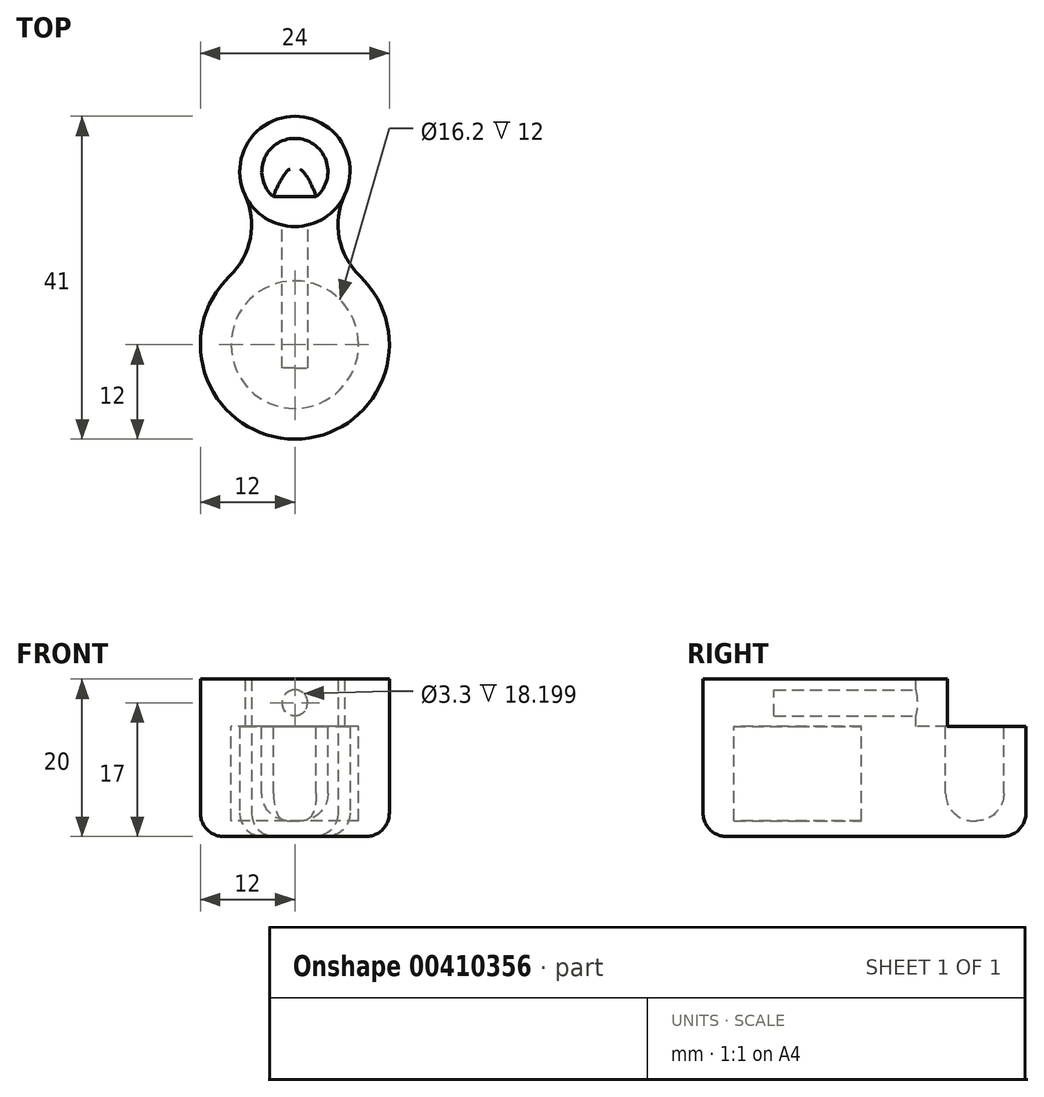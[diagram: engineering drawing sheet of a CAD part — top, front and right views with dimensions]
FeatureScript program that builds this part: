
annotation { "Feature Type Name" : "Feature", "Feature Type Description" : "" }
export const myFeature = defineFeature(function(context is Context, id is Id, definition is map)
    precondition{}
    {
        {
            var Q0;
            Q0=qCreatedBy(makeId("Top.planeOp"),FACE);
            var sketch = newSketch(context, id + "F0", { "sketchPlane" : qUnion([Q0])});
            skArc(sketch, "E0", {"start": v(0, 7) * mm, "mid": v(5.9, 3.75) * mm, "end": v(6.34, -2.97) * mm});
            skArc(sketch, "E1", {"start": v(0, -10) * mm, "mid": v(4.46, -10.86) * mm, "end": v(8.28, -13.31) * mm, "construction": true});
            skArc(sketch, "E2", {"start": v(6.34, -2.97) * mm, "mid": v(5.64, -8.46) * mm, "end": v(8.28, -13.31) * mm});
            skLineSegment(sketch, "E3", {"start": v(0, -34) * mm, "end": v(0, -10) * mm});
            skLineSegment(sketch, "E4", {"start": v(0, -10) * mm, "end": v(0, -7) * mm});
            skLineSegment(sketch, "E5", {"start": v(0, -7) * mm, "end": v(0, 7) * mm});
            skArc(sketch, "E6", {"start": v(8.28, -13.31) * mm, "mid": v(11.14, -26.46) * mm, "end": v(0, -34) * mm});
            skArc(sketch, "E7", {"start": v(6.34, -2.97) * mm, "mid": v(3.75, -5.9) * mm, "end": v(0, -7) * mm, "construction": true});
            skSolve(sketch);
        }
        {
            var Q0;
            Q0 = qSketchRegion(id + "F0", true);
            extrude(context, id + "F1", {"entities" : qUnion([Q0]), "depth" : 14 * mm});
        }
        {
            var Q0;
            Q0=makeQuery(id+"F1.opExtrude","CAP_FACE",FACE,{"disambiguationData":[OSD([sQuery(id+"F0.wireOp",EDGE,"E0"),sQuery(id+"F0.wireOp",EDGE,"E2"),sQuery(id+"F0.wireOp",EDGE,"E3"),sQuery(id+"F0.wireOp",EDGE,"E4"),sQuery(id+"F0.wireOp",EDGE,"E5"),sQuery(id+"F0.wireOp",EDGE,"E6")])],"isStart":false});
            var sketch = newSketch(context, id + "F2", { "sketchPlane" : qUnion([Q0])});
            skArc(sketch, "E8", {"start": v(0, 7) * mm, "mid": v(7, 0) * mm, "end": v(0, -7) * mm});
            skSolve(sketch);
        }
        {
            var Q0;
            {var subQ0=sQuery(id+"F2.wireOp",EDGE,"E8");var subQ3=makeQuery(id+"F2.imprint","INTERSECT",VERTEX,{"derivedFrom":[makeQuery(id+"F1.opExtrude","CAP_EDGE",EDGE,{"disambiguationData":[OSD([sQuery(id+"F0.wireOp",EDGE,"E2")])],"isStart":false}),subQ0]});Q0=makeQuery(id+"F2.imprint","IMPRINT",FACE,{"disambiguationData":[TD([[makeQuery(id+"F2.imprint","IMPRINT",EDGE,{"disambiguationData":[TD([[subQ3,1.0]])],"derivedFrom":subQ0}),-1.0]])]});}
            extrude(context, id + "F3", {"entities" : qUnion([Q0]), "operationType" : NewBodyOperationType.ADD, "depth" : 6 * mm});
        }
        {
            var Q0;
            Q0=makeQuery(id+"F1.opExtrude","SWEPT_BODY",BODY,{"disambiguationData":[OSD([sQuery(id+"F0.wireOp",EDGE,"E0"),sQuery(id+"F0.wireOp",EDGE,"E2"),sQuery(id+"F0.wireOp",EDGE,"E3"),sQuery(id+"F0.wireOp",EDGE,"E4"),sQuery(id+"F0.wireOp",EDGE,"E5"),sQuery(id+"F0.wireOp",EDGE,"E6")])]});
            var Q1;
            Q1=qCreatedBy(makeId("Right.planeOp"),FACE);
            mirror(context, id + "F4", {"operationType" : NewBodyOperationType.ADD, "entities" : qUnion([Q0]), "mirrorPlane" : qUnion([Q1])});
        }
        {
            var Q0;
            {var subQ0=makeQuery(id+"F3.opExtrude","CAP_FACE",FACE,{"disambiguationData":[OSD([sQuery(id+"F0.wireOp",EDGE,"E3"),sQuery(id+"F0.wireOp",EDGE,"E4"),sQuery(id+"F0.wireOp",EDGE,"E5"),sQuery(id+"F2.wireOp",EDGE,"E8")])],"isStart":false});Q0=makeQuery(id+"F4.boolean.opBoolean","MERGE",FACE,{"derivedFrom":[subQ0,makeQuery(id+"F4.opPattern","COPY",FACE,{"derivedFrom":subQ0,"instanceName":"1"})]});}
            var sketch = newSketch(context, id + "F5", { "sketchPlane" : qUnion([Q0])});
            skLineSegment(sketch, "E9", {"start": v(-2.72, -3.2) * mm, "end": v(2.72, -3.2) * mm});
            skArc(sketch, "E10", {"start": v(-2.72, -3.2) * mm, "mid": v(0, -4.2) * mm, "end": v(2.72, -3.2) * mm, "construction": true});
            skArc(sketch, "E11", {"start": v(2.72, -3.2) * mm, "mid": v(0, 4.2) * mm, "end": v(-2.72, -3.2) * mm});
            skSolve(sketch);
        }
        {
            var Q0;
            Q0 = qSketchRegion(id + "F5", true);
            extrude(context, id + "F6", {"entities" : qUnion([Q0]), "operationType" : NewBodyOperationType.REMOVE, "oppositeDirection" : true, "depth" : 18 * mm});
        }
        {
            var Q0;
            Q0=qCreatedBy(makeId("Front.planeOp"),FACE);
            var sketch = newSketch(context, id + "F7", { "sketchPlane" : qUnion([Q0])});
            skCircle(sketch, "E12", {"center": v(0, 17) * mm, "radius": 1.65 * mm});
            skSolve(sketch);
        }
        {
            var Q0;
            Q0 = qSketchRegion(id + "F7", true);
            extrude(context, id + "F8", {"entities" : qUnion([Q0]), "operationType" : NewBodyOperationType.REMOVE, "depth" : 25 * mm});
        }
        {
            var Q0;
            {var subQ0=makeQuery(id+"F1.opExtrude","CAP_FACE",FACE,{"disambiguationData":[OSD([sQuery(id+"F0.wireOp",EDGE,"E0"),sQuery(id+"F0.wireOp",EDGE,"E2"),sQuery(id+"F0.wireOp",EDGE,"E3"),sQuery(id+"F0.wireOp",EDGE,"E4"),sQuery(id+"F0.wireOp",EDGE,"E5"),sQuery(id+"F0.wireOp",EDGE,"E6")])],"isStart":false});Q0=makeQuery(id+"F4.boolean.opBoolean","MERGE",FACE,{"derivedFrom":[subQ0,makeQuery(id+"F4.opPattern","COPY",FACE,{"derivedFrom":subQ0,"instanceName":"1"})]});}
            var sketch = newSketch(context, id + "F9", { "sketchPlane" : qUnion([Q0])});
            skCircle(sketch, "E13", {"center": v(0, -22) * mm, "radius": 8.1 * mm});
            skSolve(sketch);
        }
        {
            var Q0;
            Q0 = qSketchRegion(id + "F9", true);
            extrude(context, id + "F10", {"entities" : qUnion([Q0]), "operationType" : NewBodyOperationType.REMOVE, "oppositeDirection" : true, "depth" : 12 * mm});
        }
        {
            var Q0;
            {var subQ0=makeQuery(id+"F1.opExtrude","CAP_EDGE",EDGE,{"disambiguationData":[OSD([sQuery(id+"F0.wireOp",EDGE,"E0")])],"isStart":true});Q0=makeQuery(id+"F4.boolean.opBoolean","MERGE",EDGE,{"derivedFrom":[subQ0,makeQuery(id+"F4.opPattern","COPY",EDGE,{"derivedFrom":subQ0,"instanceName":"1"})]});}
            var Q1;
            Q1=makeQuery(id+"F1.opExtrude","CAP_EDGE",EDGE,{"disambiguationData":[OSD([sQuery(id+"F0.wireOp",EDGE,"E2")])],"isStart":true});
            var Q2;
            {var subQ0=makeQuery(id+"F1.opExtrude","CAP_EDGE",EDGE,{"disambiguationData":[OSD([sQuery(id+"F0.wireOp",EDGE,"E6")])],"isStart":true});Q2=makeQuery(id+"F4.boolean.opBoolean","MERGE",EDGE,{"derivedFrom":[subQ0,makeQuery(id+"F4.opPattern","COPY",EDGE,{"derivedFrom":subQ0,"instanceName":"1"})]});}
            var Q3;
            Q3=makeQuery(id+"F4.opPattern","COPY",EDGE,{"derivedFrom":makeQuery(id+"F1.opExtrude","CAP_EDGE",EDGE,{"disambiguationData":[OSD([sQuery(id+"F0.wireOp",EDGE,"E2")])],"isStart":true}),"instanceName":"1"});
            var Q4;
            {var subQ0=makeQuery(id+"F1.opExtrude","CAP_EDGE",EDGE,{"disambiguationData":[OSD([sQuery(id+"F0.wireOp",EDGE,"E6")])],"isStart":false});Q4=makeQuery(id+"F4.boolean.opBoolean","MERGE",EDGE,{"derivedFrom":[subQ0,makeQuery(id+"F4.opPattern","COPY",EDGE,{"derivedFrom":subQ0,"instanceName":"1"})]});}
            fillet(context, id + "F11", {"entities" : qUnion([Q0, Q1, Q2, Q3, Q4]), "radius" : 3 * mm, "tangentPropagation" : true, "allowEdgeOverflow" : false});
        }
        {
            var Q0;
            Q0=makeQuery(id+"F6.boolean.opBoolean","COPY",FACE,{"derivedFrom":makeQuery(id+"F6.opExtrude","CAP_FACE",FACE,{"disambiguationData":[OSD([sQuery(id+"F5.wireOp",EDGE,"E9"),sQuery(id+"F5.wireOp",EDGE,"E11")])],"isStart":false})});
            fillet(context, id + "F12", {"entities" : qUnion([Q0]), "radius" : 3.5 * mm, "tangentPropagation" : true, "allowEdgeOverflow" : false});
        }
    });
